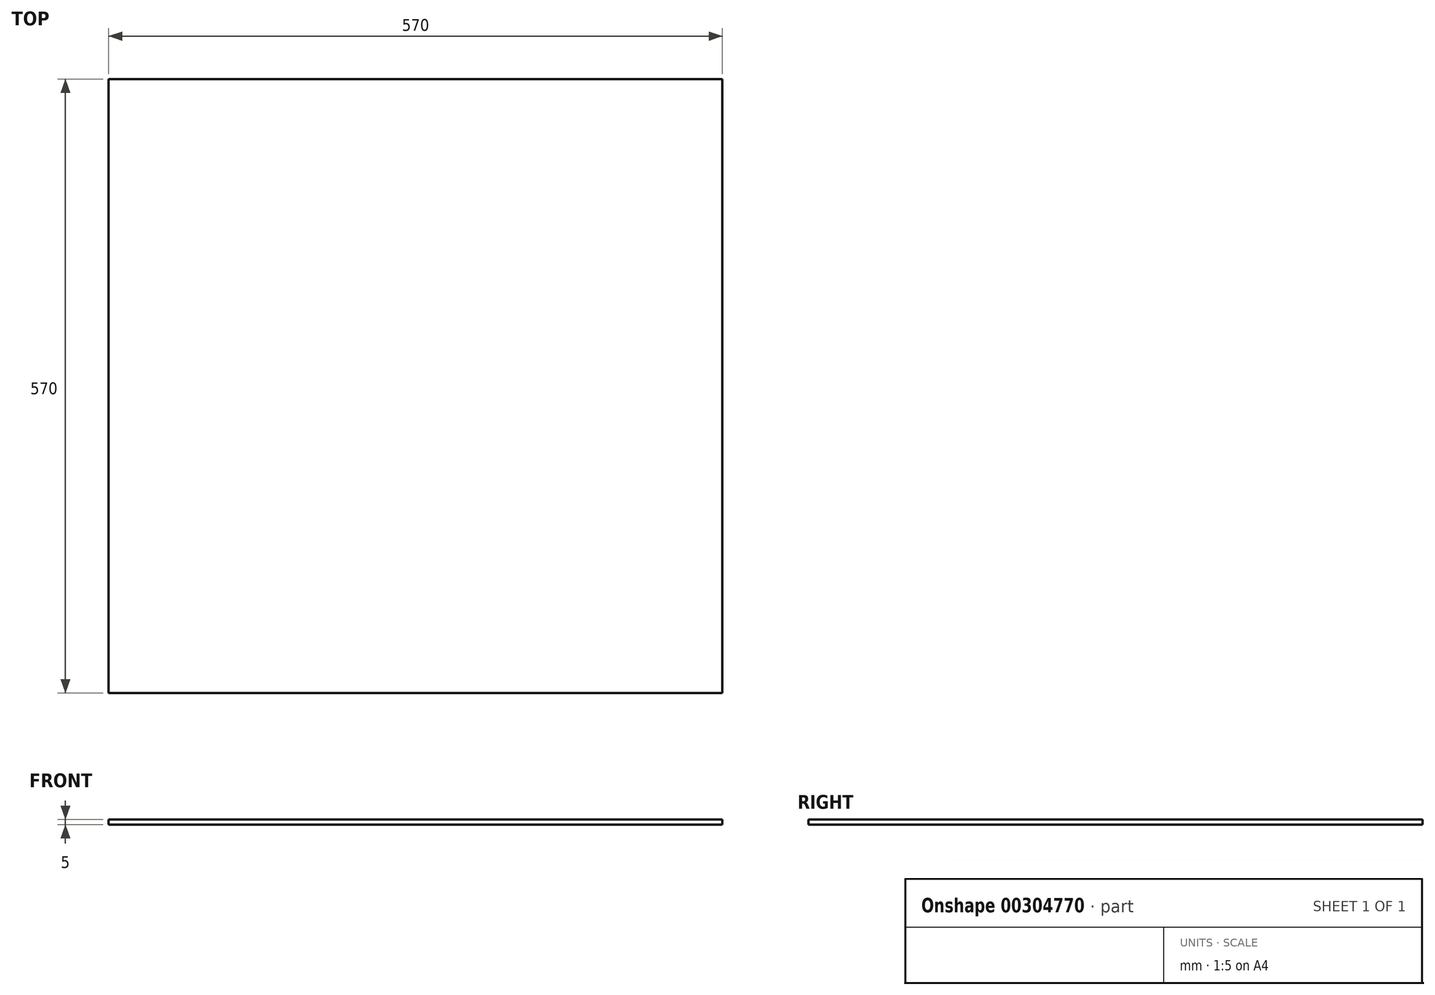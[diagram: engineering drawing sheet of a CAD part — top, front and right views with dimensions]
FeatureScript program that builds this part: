
annotation { "Feature Type Name" : "Feature", "Feature Type Description" : "" }
export const myFeature = defineFeature(function(context is Context, id is Id, definition is map)
    precondition{}
    {
        {
            var Q0;
            Q0=qCreatedBy(makeId("Top.planeOp"),FACE);
            var sketch = newSketch(context, id + "F0", { "sketchPlane" : qUnion([Q0])});
            skLineSegment(sketch, "E0.bottom", {"start": v(-285, 285) * mm, "end": v(285, 285) * mm});
            skLineSegment(sketch, "E0.top", {"start": v(-285, -285) * mm, "end": v(285, -285) * mm});
            skLineSegment(sketch, "E0.left", {"start": v(-285, 285) * mm, "end": v(-285, -285) * mm});
            skLineSegment(sketch, "E0.right", {"start": v(285, 285) * mm, "end": v(285, -285) * mm});
            skPoint(sketch, "E0.middle", {"position": v(0, 0) * mm});
            skSolve(sketch);
        }
        {
            var Q0;
            Q0=makeQuery(id+"F0.imprint","IMPRINT",FACE,{"disambiguationData":[TD([[makeQuery(id+"F0.imprint","IMPRINT",EDGE,{"derivedFrom":sQuery(id+"F0.wireOp",EDGE,"E0.bottom")}),-1.0]])]});
            extrude(context, id + "F1", {"entities" : qUnion([Q0]), "depth" : 5 * mm});
        }
    });
